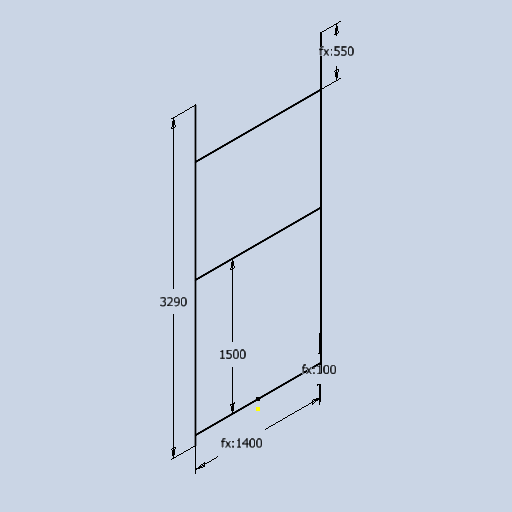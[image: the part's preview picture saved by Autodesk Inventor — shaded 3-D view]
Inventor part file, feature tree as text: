
AUTODESK INVENTOR PART (.ipt)
format: ipt  version: 2025 (Build 290162010, 162A)  size: 262,656 bytes
history: native  units: mm
features: sketch x1
ambient origin geometry x8: Origin, YZ Plane, XZ Plane, XY Plane, X Axis, Y Axis, Z Axis, Center Point
feature tree (1):
  sketch  "Sketch2"  dims[d4=3290.0mm d5=1400.0mm d6=550.0mm d7=100.0mm d8=1500.0mm]
